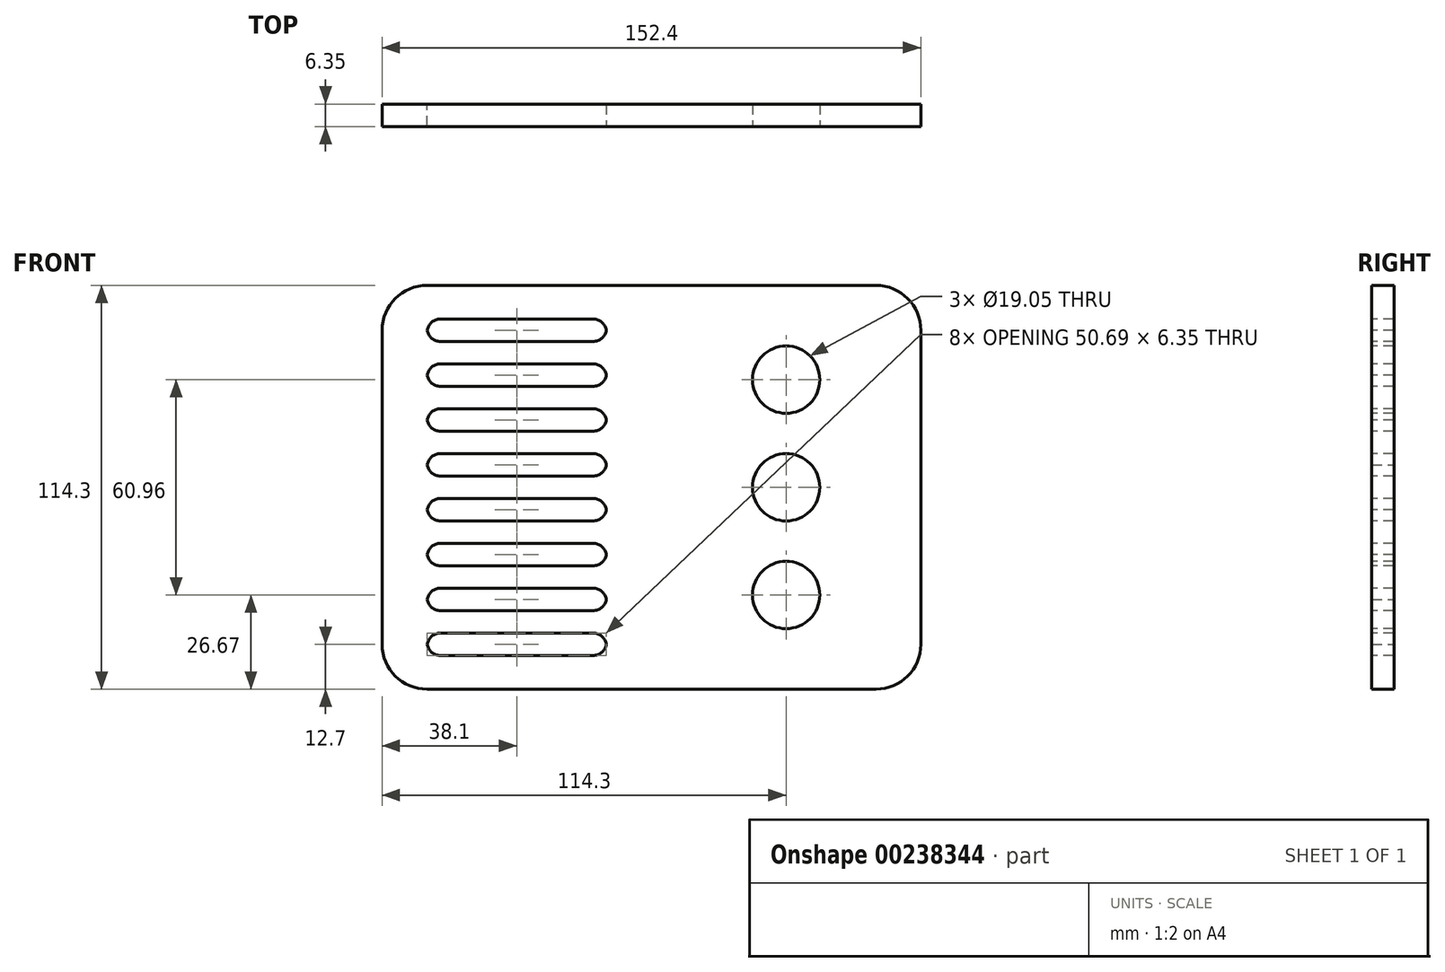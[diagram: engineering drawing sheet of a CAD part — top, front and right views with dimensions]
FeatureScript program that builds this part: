
annotation { "Feature Type Name" : "Feature", "Feature Type Description" : "" }
export const myFeature = defineFeature(function(context is Context, id is Id, definition is map)
    precondition{}
    {
        {
            var Q0;
            Q0=qCreatedBy(makeId("Front.planeOp"),FACE);
            var sketch = newSketch(context, id + "F0", { "sketchPlane" : qUnion([Q0])});
            skLineSegment(sketch, "E0.bottom", {"start": v(-76.2, 57.15) * mm, "end": v(76.2, 57.15) * mm});
            skLineSegment(sketch, "E0.top", {"start": v(-76.2, -57.15) * mm, "end": v(76.2, -57.15) * mm});
            skLineSegment(sketch, "E0.left", {"start": v(-76.2, 57.15) * mm, "end": v(-76.2, -57.15) * mm});
            skLineSegment(sketch, "E0.right", {"start": v(76.2, 57.15) * mm, "end": v(76.2, -57.15) * mm});
            skPoint(sketch, "E0.middle", {"position": v(0, 0) * mm});
            skSolve(sketch);
        }
        {
            var Q0;
            Q0=makeQuery(id+"F0.imprint","IMPRINT",FACE,{"disambiguationData":[TD([[makeQuery(id+"F0.imprint","IMPRINT",EDGE,{"derivedFrom":sQuery(id+"F0.wireOp",EDGE,"E0.bottom")}),-1.0]])]});
            extrude(context, id + "F1", {"entities" : qUnion([Q0]), "depth" : 6.35 * mm});
        }
        {
            var Q0;
            Q0=makeQuery(id+"F1.opExtrude","SWEPT_EDGE",EDGE,{"disambiguationData":[OSD([sQuery(id+"F0.wireOp",EDGE,"E0.bottom"),sQuery(id+"F0.wireOp",EDGE,"E0.left")])]});
            var Q1;
            Q1=makeQuery(id+"F1.opExtrude","SWEPT_EDGE",EDGE,{"disambiguationData":[OSD([sQuery(id+"F0.wireOp",EDGE,"E0.top"),sQuery(id+"F0.wireOp",EDGE,"E0.left")])]});
            var Q2;
            Q2=makeQuery(id+"F1.opExtrude","SWEPT_EDGE",EDGE,{"disambiguationData":[OSD([sQuery(id+"F0.wireOp",EDGE,"E0.top"),sQuery(id+"F0.wireOp",EDGE,"E0.right")])]});
            var Q3;
            Q3=makeQuery(id+"F1.opExtrude","SWEPT_EDGE",EDGE,{"disambiguationData":[OSD([sQuery(id+"F0.wireOp",EDGE,"E0.bottom"),sQuery(id+"F0.wireOp",EDGE,"E0.right")])]});
            fillet(context, id + "F2", {"entities" : qUnion([Q0, Q1, Q2, Q3]), "radius" : 12.7 * mm, "tangentPropagation" : true, "allowEdgeOverflow" : false});
        }
        {
            var Q0;
            Q0=makeQuery(id+"F1.opExtrude","CAP_FACE",FACE,{"disambiguationData":[OSD([sQuery(id+"F0.wireOp",EDGE,"E0.bottom"),sQuery(id+"F0.wireOp",EDGE,"E0.top"),sQuery(id+"F0.wireOp",EDGE,"E0.left"),sQuery(id+"F0.wireOp",EDGE,"E0.right")])],"isStart":false});
            var sketch = newSketch(context, id + "F3", { "sketchPlane" : qUnion([Q0])});
            skCircle(sketch, "E1", {"center": v(38.1, 30.48) * mm, "radius": 9.53 * mm});
            skSolve(sketch);
        }
        {
            var Q0;
            Q0=makeQuery(id+"F3.imprint","IMPRINT",FACE,{"disambiguationData":[TD([[makeQuery(id+"F3.imprint","IMPRINT",EDGE,{"derivedFrom":sQuery(id+"F3.wireOp",EDGE,"E1")}),1.0]])]});
            extrude(context, id + "F4", {"entities" : qUnion([Q0]), "operationType" : NewBodyOperationType.REMOVE, "oppositeDirection" : true, "depth" : 25.4 * mm});
        }
        {
            var Q0;
            Q0=makeQuery(id+"F1.opExtrude","CAP_FACE",FACE,{"disambiguationData":[OSD([sQuery(id+"F0.wireOp",EDGE,"E0.bottom"),sQuery(id+"F0.wireOp",EDGE,"E0.top"),sQuery(id+"F0.wireOp",EDGE,"E0.left"),sQuery(id+"F0.wireOp",EDGE,"E0.right")])],"isStart":false});
            var sketch = newSketch(context, id + "F5", { "sketchPlane" : qUnion([Q0])});
            skCircle(sketch, "E2", {"center": v(38.1, 0) * mm, "radius": 9.53 * mm});
            skSolve(sketch);
        }
        {
            var Q0;
            Q0=makeQuery(id+"F5.imprint","IMPRINT",FACE,{"disambiguationData":[TD([[makeQuery(id+"F5.imprint","IMPRINT",EDGE,{"derivedFrom":sQuery(id+"F5.wireOp",EDGE,"E2")}),1.0]])]});
            extrude(context, id + "F6", {"entities" : qUnion([Q0]), "operationType" : NewBodyOperationType.REMOVE, "oppositeDirection" : true, "depth" : 25.4 * mm});
        }
        {
            var Q0;
            Q0=makeQuery(id+"F1.opExtrude","CAP_FACE",FACE,{"disambiguationData":[OSD([sQuery(id+"F0.wireOp",EDGE,"E0.bottom"),sQuery(id+"F0.wireOp",EDGE,"E0.top"),sQuery(id+"F0.wireOp",EDGE,"E0.left"),sQuery(id+"F0.wireOp",EDGE,"E0.right")])],"isStart":false});
            var sketch = newSketch(context, id + "F7", { "sketchPlane" : qUnion([Q0])});
            skCircle(sketch, "E3", {"center": v(38.1, -30.48) * mm, "radius": 9.53 * mm});
            skSolve(sketch);
        }
        {
            var Q0;
            Q0=makeQuery(id+"F7.imprint","IMPRINT",FACE,{"disambiguationData":[TD([[makeQuery(id+"F7.imprint","IMPRINT",EDGE,{"derivedFrom":sQuery(id+"F7.wireOp",EDGE,"E3")}),1.0]])]});
            extrude(context, id + "F8", {"entities" : qUnion([Q0]), "operationType" : NewBodyOperationType.REMOVE, "oppositeDirection" : true, "depth" : 25.4 * mm});
        }
        {
            var Q0;
            Q0=makeQuery(id+"F1.opExtrude","CAP_FACE",FACE,{"disambiguationData":[OSD([sQuery(id+"F0.wireOp",EDGE,"E0.bottom"),sQuery(id+"F0.wireOp",EDGE,"E0.top"),sQuery(id+"F0.wireOp",EDGE,"E0.left"),sQuery(id+"F0.wireOp",EDGE,"E0.right")])],"isStart":false});
            var sketch = newSketch(context, id + "F9", { "sketchPlane" : qUnion([Q0])});
            skLineSegment(sketch, "E4.bottom", {"start": v(-12.7, -41.28) * mm, "end": v(-63.5, -41.28) * mm});
            skLineSegment(sketch, "E4.top", {"start": v(-12.7, -47.63) * mm, "end": v(-63.5, -47.63) * mm});
            skLineSegment(sketch, "E4.left", {"start": v(-12.7, -41.28) * mm, "end": v(-12.7, -47.63) * mm});
            skLineSegment(sketch, "E4.right", {"start": v(-63.5, -41.28) * mm, "end": v(-63.5, -47.63) * mm});
            skPoint(sketch, "E4.middle", {"position": v(-38.1, -44.45) * mm});
            skSolve(sketch);
        }
        {
            var Q0;
            Q0=makeQuery(id+"F9.imprint","IMPRINT",FACE,{"disambiguationData":[TD([[makeQuery(id+"F9.imprint","IMPRINT",EDGE,{"derivedFrom":sQuery(id+"F9.wireOp",EDGE,"E4.bottom")}),-1.0]])]});
            var sketch = newSketch(context, id + "F10", { "sketchPlane" : qUnion([Q0])});
            skLineSegment(sketch, "E5.bottom", {"start": v(-12.7, -28.58) * mm, "end": v(-63.5, -28.58) * mm});
            skLineSegment(sketch, "E5.top", {"start": v(-12.7, -34.93) * mm, "end": v(-63.5, -34.93) * mm});
            skLineSegment(sketch, "E5.left", {"start": v(-12.7, -28.58) * mm, "end": v(-12.7, -34.93) * mm});
            skLineSegment(sketch, "E5.right", {"start": v(-63.5, -28.58) * mm, "end": v(-63.5, -34.93) * mm});
            skPoint(sketch, "E5.middle", {"position": v(-38.1, -31.75) * mm});
            skSolve(sketch);
        }
        {
            var Q0;
            Q0=makeQuery(id+"F9.imprint","IMPRINT",FACE,{"disambiguationData":[TD([[makeQuery(id+"F9.imprint","IMPRINT",EDGE,{"derivedFrom":sQuery(id+"F9.wireOp",EDGE,"E4.bottom")}),-1.0]])]});
            var sketch = newSketch(context, id + "F11", { "sketchPlane" : qUnion([Q0])});
            skLineSegment(sketch, "E6.bottom", {"start": v(-12.7, -22.23) * mm, "end": v(-63.5, -22.23) * mm});
            skLineSegment(sketch, "E6.top", {"start": v(-12.7, -15.88) * mm, "end": v(-63.5, -15.88) * mm});
            skLineSegment(sketch, "E6.left", {"start": v(-12.7, -22.23) * mm, "end": v(-12.7, -15.88) * mm});
            skLineSegment(sketch, "E6.right", {"start": v(-63.5, -22.23) * mm, "end": v(-63.5, -15.88) * mm});
            skPoint(sketch, "E6.middle", {"position": v(-38.1, -19.05) * mm});
            skSolve(sketch);
        }
        {
            var Q0;
            Q0=makeQuery(id+"F9.imprint","IMPRINT",FACE,{"disambiguationData":[TD([[makeQuery(id+"F9.imprint","IMPRINT",EDGE,{"derivedFrom":sQuery(id+"F9.wireOp",EDGE,"E4.bottom")}),-1.0]])]});
            var sketch = newSketch(context, id + "F12", { "sketchPlane" : qUnion([Q0])});
            skLineSegment(sketch, "E7.bottom", {"start": v(-12.7, -9.53) * mm, "end": v(-63.5, -9.53) * mm});
            skLineSegment(sketch, "E7.top", {"start": v(-12.7, -3.18) * mm, "end": v(-63.5, -3.18) * mm});
            skLineSegment(sketch, "E7.left", {"start": v(-12.7, -9.53) * mm, "end": v(-12.7, -3.18) * mm});
            skLineSegment(sketch, "E7.right", {"start": v(-63.5, -9.53) * mm, "end": v(-63.5, -3.18) * mm});
            skPoint(sketch, "E7.middle", {"position": v(-38.1, -6.35) * mm});
            skSolve(sketch);
        }
        {
            var Q0;
            Q0=makeQuery(id+"F9.imprint","IMPRINT",FACE,{"disambiguationData":[TD([[makeQuery(id+"F9.imprint","IMPRINT",EDGE,{"derivedFrom":sQuery(id+"F9.wireOp",EDGE,"E4.bottom")}),-1.0]])]});
            var sketch = newSketch(context, id + "F13", { "sketchPlane" : qUnion([Q0])});
            skLineSegment(sketch, "E8.bottom", {"start": v(-12.7, 9.53) * mm, "end": v(-63.5, 9.52) * mm});
            skLineSegment(sketch, "E8.top", {"start": v(-12.7, 3.17) * mm, "end": v(-63.5, 3.17) * mm});
            skLineSegment(sketch, "E8.left", {"start": v(-12.7, 9.53) * mm, "end": v(-12.7, 3.17) * mm});
            skLineSegment(sketch, "E8.right", {"start": v(-63.5, 9.52) * mm, "end": v(-63.5, 3.17) * mm});
            skPoint(sketch, "E8.middle", {"position": v(-38.1, 6.35) * mm});
            skSolve(sketch);
        }
        {
            var Q0;
            Q0=makeQuery(id+"F9.imprint","IMPRINT",FACE,{"disambiguationData":[TD([[makeQuery(id+"F9.imprint","IMPRINT",EDGE,{"derivedFrom":sQuery(id+"F9.wireOp",EDGE,"E4.bottom")}),-1.0]])]});
            var sketch = newSketch(context, id + "F14", { "sketchPlane" : qUnion([Q0])});
            skLineSegment(sketch, "E9.bottom", {"start": v(-12.7, 15.88) * mm, "end": v(-63.5, 15.87) * mm});
            skLineSegment(sketch, "E9.top", {"start": v(-12.7, 22.22) * mm, "end": v(-63.5, 22.22) * mm});
            skLineSegment(sketch, "E9.left", {"start": v(-12.7, 15.88) * mm, "end": v(-12.7, 22.22) * mm});
            skLineSegment(sketch, "E9.right", {"start": v(-63.5, 15.88) * mm, "end": v(-63.5, 22.22) * mm});
            skPoint(sketch, "E9.middle", {"position": v(-38.1, 19.05) * mm});
            skSolve(sketch);
        }
        {
            var Q0;
            Q0=makeQuery(id+"F9.imprint","IMPRINT",FACE,{"disambiguationData":[TD([[makeQuery(id+"F9.imprint","IMPRINT",EDGE,{"derivedFrom":sQuery(id+"F9.wireOp",EDGE,"E4.bottom")}),-1.0]])]});
            var sketch = newSketch(context, id + "F15", { "sketchPlane" : qUnion([Q0])});
            skLineSegment(sketch, "E10.bottom", {"start": v(-12.7, 28.58) * mm, "end": v(-63.5, 28.57) * mm});
            skLineSegment(sketch, "E10.top", {"start": v(-12.7, 34.93) * mm, "end": v(-63.5, 34.92) * mm});
            skLineSegment(sketch, "E10.left", {"start": v(-12.7, 28.58) * mm, "end": v(-12.7, 34.93) * mm});
            skLineSegment(sketch, "E10.right", {"start": v(-63.5, 28.57) * mm, "end": v(-63.5, 34.92) * mm});
            skPoint(sketch, "E10.middle", {"position": v(-38.1, 31.75) * mm});
            skSolve(sketch);
        }
        {
            var Q0;
            Q0=makeQuery(id+"F9.imprint","IMPRINT",FACE,{"disambiguationData":[TD([[makeQuery(id+"F9.imprint","IMPRINT",EDGE,{"derivedFrom":sQuery(id+"F9.wireOp",EDGE,"E4.bottom")}),-1.0]])]});
            var sketch = newSketch(context, id + "F16", { "sketchPlane" : qUnion([Q0])});
            skLineSegment(sketch, "E11.bottom", {"start": v(-12.7, 41.28) * mm, "end": v(-63.5, 41.27) * mm});
            skLineSegment(sketch, "E11.top", {"start": v(-12.7, 47.63) * mm, "end": v(-63.5, 47.62) * mm});
            skLineSegment(sketch, "E11.left", {"start": v(-12.7, 41.28) * mm, "end": v(-12.7, 47.63) * mm});
            skLineSegment(sketch, "E11.right", {"start": v(-63.5, 41.27) * mm, "end": v(-63.5, 47.62) * mm});
            skPoint(sketch, "E11.middle", {"position": v(-38.1, 44.45) * mm});
            skSolve(sketch);
        }
        {
            var Q0;
            Q0=makeQuery(id+"F16.imprint","IMPRINT",FACE,{"disambiguationData":[TD([[makeQuery(id+"F16.imprint","IMPRINT",EDGE,{"derivedFrom":sQuery(id+"F16.wireOp",EDGE,"E11.bottom")}),-1.0]])]});
            var Q1;
            Q1=makeQuery(id+"F15.imprint","IMPRINT",FACE,{"disambiguationData":[TD([[makeQuery(id+"F15.imprint","IMPRINT",EDGE,{"derivedFrom":sQuery(id+"F15.wireOp",EDGE,"E10.bottom")}),-1.0]])]});
            var Q2;
            Q2=makeQuery(id+"F14.imprint","IMPRINT",FACE,{"disambiguationData":[TD([[makeQuery(id+"F14.imprint","IMPRINT",EDGE,{"derivedFrom":sQuery(id+"F14.wireOp",EDGE,"E9.bottom")}),-1.0]])]});
            var Q3;
            Q3=makeQuery(id+"F13.imprint","IMPRINT",FACE,{"disambiguationData":[TD([[makeQuery(id+"F13.imprint","IMPRINT",EDGE,{"derivedFrom":sQuery(id+"F13.wireOp",EDGE,"E8.bottom")}),1.0]])]});
            var Q4;
            Q4=makeQuery(id+"F12.imprint","IMPRINT",FACE,{"disambiguationData":[TD([[makeQuery(id+"F12.imprint","IMPRINT",EDGE,{"derivedFrom":sQuery(id+"F12.wireOp",EDGE,"E7.bottom")}),-1.0]])]});
            var Q5;
            Q5=makeQuery(id+"F11.imprint","IMPRINT",FACE,{"disambiguationData":[TD([[makeQuery(id+"F11.imprint","IMPRINT",EDGE,{"derivedFrom":sQuery(id+"F11.wireOp",EDGE,"E6.bottom")}),-1.0]])]});
            var Q6;
            Q6=makeQuery(id+"F10.imprint","IMPRINT",FACE,{"disambiguationData":[TD([[makeQuery(id+"F10.imprint","IMPRINT",EDGE,{"derivedFrom":sQuery(id+"F10.wireOp",EDGE,"E5.bottom")}),1.0]])]});
            var Q7;
            Q7=makeQuery(id+"F9.imprint","IMPRINT",FACE,{"disambiguationData":[TD([[makeQuery(id+"F9.imprint","IMPRINT",EDGE,{"derivedFrom":sQuery(id+"F9.wireOp",EDGE,"E4.bottom")}),1.0]])]});
            extrude(context, id + "F17", {"entities" : qUnion([Q0, Q1, Q2, Q3, Q4, Q5, Q6, Q7]), "operationType" : NewBodyOperationType.REMOVE, "oppositeDirection" : true, "depth" : 25.4 * mm});
        }
        {
            var Q0;
            Q0=makeQuery(id+"F17.boolean.opBoolean","COPY",EDGE,{"derivedFrom":makeQuery(id+"F17.opExtrude","SWEPT_EDGE",EDGE,{"disambiguationData":[OSD([sQuery(id+"F13.wireOp",EDGE,"E8.top"),sQuery(id+"F13.wireOp",EDGE,"E8.left")])]})});
            var Q1;
            Q1=makeQuery(id+"F17.boolean.opBoolean","COPY",EDGE,{"derivedFrom":makeQuery(id+"F17.opExtrude","SWEPT_EDGE",EDGE,{"disambiguationData":[OSD([sQuery(id+"F12.wireOp",EDGE,"E7.bottom"),sQuery(id+"F12.wireOp",EDGE,"E7.left")])]})});
            var Q2;
            Q2=makeQuery(id+"F17.boolean.opBoolean","COPY",EDGE,{"derivedFrom":makeQuery(id+"F17.opExtrude","SWEPT_EDGE",EDGE,{"disambiguationData":[OSD([sQuery(id+"F10.wireOp",EDGE,"E5.top"),sQuery(id+"F10.wireOp",EDGE,"E5.left")])]})});
            var Q3;
            Q3=makeQuery(id+"F17.boolean.opBoolean","COPY",EDGE,{"derivedFrom":makeQuery(id+"F17.opExtrude","SWEPT_EDGE",EDGE,{"disambiguationData":[OSD([sQuery(id+"F11.wireOp",EDGE,"E6.bottom"),sQuery(id+"F11.wireOp",EDGE,"E6.left")])]})});
            var Q4;
            Q4=makeQuery(id+"F17.boolean.opBoolean","COPY",EDGE,{"derivedFrom":makeQuery(id+"F17.opExtrude","SWEPT_EDGE",EDGE,{"disambiguationData":[OSD([sQuery(id+"F9.wireOp",EDGE,"E4.top"),sQuery(id+"F9.wireOp",EDGE,"E4.left")])]})});
            var Q5;
            Q5=makeQuery(id+"F17.boolean.opBoolean","COPY",EDGE,{"derivedFrom":makeQuery(id+"F17.opExtrude","SWEPT_EDGE",EDGE,{"disambiguationData":[OSD([sQuery(id+"F14.wireOp",EDGE,"E9.bottom"),sQuery(id+"F14.wireOp",EDGE,"E9.left")])]})});
            var Q6;
            Q6=makeQuery(id+"F17.boolean.opBoolean","COPY",EDGE,{"derivedFrom":makeQuery(id+"F17.opExtrude","SWEPT_EDGE",EDGE,{"disambiguationData":[OSD([sQuery(id+"F15.wireOp",EDGE,"E10.bottom"),sQuery(id+"F15.wireOp",EDGE,"E10.left")])]})});
            var Q7;
            Q7=makeQuery(id+"F17.boolean.opBoolean","COPY",EDGE,{"derivedFrom":makeQuery(id+"F17.opExtrude","SWEPT_EDGE",EDGE,{"disambiguationData":[OSD([sQuery(id+"F16.wireOp",EDGE,"E11.bottom"),sQuery(id+"F16.wireOp",EDGE,"E11.left")])]})});
            var Q8;
            Q8=makeQuery(id+"F17.boolean.opBoolean","COPY",EDGE,{"derivedFrom":makeQuery(id+"F17.opExtrude","SWEPT_EDGE",EDGE,{"disambiguationData":[OSD([sQuery(id+"F9.wireOp",EDGE,"E4.bottom"),sQuery(id+"F9.wireOp",EDGE,"E4.left")])]})});
            var Q9;
            Q9=makeQuery(id+"F17.boolean.opBoolean","COPY",EDGE,{"derivedFrom":makeQuery(id+"F17.opExtrude","SWEPT_EDGE",EDGE,{"disambiguationData":[OSD([sQuery(id+"F10.wireOp",EDGE,"E5.bottom"),sQuery(id+"F10.wireOp",EDGE,"E5.left")])]})});
            var Q10;
            Q10=makeQuery(id+"F17.boolean.opBoolean","COPY",EDGE,{"derivedFrom":makeQuery(id+"F17.opExtrude","SWEPT_EDGE",EDGE,{"disambiguationData":[OSD([sQuery(id+"F11.wireOp",EDGE,"E6.top"),sQuery(id+"F11.wireOp",EDGE,"E6.left")])]})});
            var Q11;
            Q11=makeQuery(id+"F17.boolean.opBoolean","COPY",EDGE,{"derivedFrom":makeQuery(id+"F17.opExtrude","SWEPT_EDGE",EDGE,{"disambiguationData":[OSD([sQuery(id+"F12.wireOp",EDGE,"E7.top"),sQuery(id+"F12.wireOp",EDGE,"E7.left")])]})});
            var Q12;
            Q12=makeQuery(id+"F17.boolean.opBoolean","COPY",EDGE,{"derivedFrom":makeQuery(id+"F17.opExtrude","SWEPT_EDGE",EDGE,{"disambiguationData":[OSD([sQuery(id+"F13.wireOp",EDGE,"E8.bottom"),sQuery(id+"F13.wireOp",EDGE,"E8.left")])]})});
            var Q13;
            Q13=makeQuery(id+"F17.boolean.opBoolean","COPY",EDGE,{"derivedFrom":makeQuery(id+"F17.opExtrude","SWEPT_EDGE",EDGE,{"disambiguationData":[OSD([sQuery(id+"F14.wireOp",EDGE,"E9.top"),sQuery(id+"F14.wireOp",EDGE,"E9.left")])]})});
            var Q14;
            Q14=makeQuery(id+"F17.boolean.opBoolean","COPY",EDGE,{"derivedFrom":makeQuery(id+"F17.opExtrude","SWEPT_EDGE",EDGE,{"disambiguationData":[OSD([sQuery(id+"F15.wireOp",EDGE,"E10.top"),sQuery(id+"F15.wireOp",EDGE,"E10.left")])]})});
            var Q15;
            Q15=makeQuery(id+"F17.boolean.opBoolean","COPY",EDGE,{"derivedFrom":makeQuery(id+"F17.opExtrude","SWEPT_EDGE",EDGE,{"disambiguationData":[OSD([sQuery(id+"F16.wireOp",EDGE,"E11.top"),sQuery(id+"F16.wireOp",EDGE,"E11.left")])]})});
            fillet(context, id + "F18", {"entities" : qUnion([Q0, Q1, Q2, Q3, Q4, Q5, Q6, Q7, Q8, Q9, Q10, Q11, Q12, Q13, Q14, Q15]), "radius" : 3.8 * mm, "tangentPropagation" : true, "allowEdgeOverflow" : false});
        }
        {
            var Q0;
            Q0=makeQuery(id+"F17.boolean.opBoolean","COPY",EDGE,{"derivedFrom":makeQuery(id+"F17.opExtrude","SWEPT_EDGE",EDGE,{"disambiguationData":[OSD([sQuery(id+"F16.wireOp",EDGE,"E11.top"),sQuery(id+"F16.wireOp",EDGE,"E11.right")])]})});
            var Q1;
            Q1=makeQuery(id+"F17.boolean.opBoolean","COPY",EDGE,{"derivedFrom":makeQuery(id+"F17.opExtrude","SWEPT_EDGE",EDGE,{"disambiguationData":[OSD([sQuery(id+"F15.wireOp",EDGE,"E10.top"),sQuery(id+"F15.wireOp",EDGE,"E10.right")])]})});
            var Q2;
            Q2=makeQuery(id+"F17.boolean.opBoolean","COPY",EDGE,{"derivedFrom":makeQuery(id+"F17.opExtrude","SWEPT_EDGE",EDGE,{"disambiguationData":[OSD([sQuery(id+"F14.wireOp",EDGE,"E9.top"),sQuery(id+"F14.wireOp",EDGE,"E9.right")])]})});
            var Q3;
            Q3=makeQuery(id+"F17.boolean.opBoolean","COPY",EDGE,{"derivedFrom":makeQuery(id+"F17.opExtrude","SWEPT_EDGE",EDGE,{"disambiguationData":[OSD([sQuery(id+"F13.wireOp",EDGE,"E8.bottom"),sQuery(id+"F13.wireOp",EDGE,"E8.right")])]})});
            var Q4;
            Q4=makeQuery(id+"F17.boolean.opBoolean","COPY",EDGE,{"derivedFrom":makeQuery(id+"F17.opExtrude","SWEPT_EDGE",EDGE,{"disambiguationData":[OSD([sQuery(id+"F12.wireOp",EDGE,"E7.top"),sQuery(id+"F12.wireOp",EDGE,"E7.right")])]})});
            var Q5;
            Q5=makeQuery(id+"F17.boolean.opBoolean","COPY",EDGE,{"derivedFrom":makeQuery(id+"F17.opExtrude","SWEPT_EDGE",EDGE,{"disambiguationData":[OSD([sQuery(id+"F11.wireOp",EDGE,"E6.top"),sQuery(id+"F11.wireOp",EDGE,"E6.right")])]})});
            var Q6;
            Q6=makeQuery(id+"F17.boolean.opBoolean","COPY",EDGE,{"derivedFrom":makeQuery(id+"F17.opExtrude","SWEPT_EDGE",EDGE,{"disambiguationData":[OSD([sQuery(id+"F10.wireOp",EDGE,"E5.bottom"),sQuery(id+"F10.wireOp",EDGE,"E5.right")])]})});
            var Q7;
            Q7=makeQuery(id+"F17.boolean.opBoolean","COPY",EDGE,{"derivedFrom":makeQuery(id+"F17.opExtrude","SWEPT_EDGE",EDGE,{"disambiguationData":[OSD([sQuery(id+"F9.wireOp",EDGE,"E4.bottom"),sQuery(id+"F9.wireOp",EDGE,"E4.right")])]})});
            var Q8;
            Q8=makeQuery(id+"F17.boolean.opBoolean","COPY",EDGE,{"derivedFrom":makeQuery(id+"F17.opExtrude","SWEPT_EDGE",EDGE,{"disambiguationData":[OSD([sQuery(id+"F16.wireOp",EDGE,"E11.bottom"),sQuery(id+"F16.wireOp",EDGE,"E11.right")])]})});
            var Q9;
            Q9=makeQuery(id+"F17.boolean.opBoolean","COPY",EDGE,{"derivedFrom":makeQuery(id+"F17.opExtrude","SWEPT_EDGE",EDGE,{"disambiguationData":[OSD([sQuery(id+"F15.wireOp",EDGE,"E10.bottom"),sQuery(id+"F15.wireOp",EDGE,"E10.right")])]})});
            var Q10;
            Q10=makeQuery(id+"F17.boolean.opBoolean","COPY",EDGE,{"derivedFrom":makeQuery(id+"F17.opExtrude","SWEPT_EDGE",EDGE,{"disambiguationData":[OSD([sQuery(id+"F14.wireOp",EDGE,"E9.bottom"),sQuery(id+"F14.wireOp",EDGE,"E9.right")])]})});
            var Q11;
            Q11=makeQuery(id+"F17.boolean.opBoolean","COPY",EDGE,{"derivedFrom":makeQuery(id+"F17.opExtrude","SWEPT_EDGE",EDGE,{"disambiguationData":[OSD([sQuery(id+"F13.wireOp",EDGE,"E8.top"),sQuery(id+"F13.wireOp",EDGE,"E8.right")])]})});
            var Q12;
            Q12=makeQuery(id+"F17.boolean.opBoolean","COPY",EDGE,{"derivedFrom":makeQuery(id+"F17.opExtrude","SWEPT_EDGE",EDGE,{"disambiguationData":[OSD([sQuery(id+"F12.wireOp",EDGE,"E7.bottom"),sQuery(id+"F12.wireOp",EDGE,"E7.right")])]})});
            var Q13;
            Q13=makeQuery(id+"F17.boolean.opBoolean","COPY",EDGE,{"derivedFrom":makeQuery(id+"F17.opExtrude","SWEPT_EDGE",EDGE,{"disambiguationData":[OSD([sQuery(id+"F11.wireOp",EDGE,"E6.bottom"),sQuery(id+"F11.wireOp",EDGE,"E6.right")])]})});
            var Q14;
            Q14=makeQuery(id+"F17.boolean.opBoolean","COPY",EDGE,{"derivedFrom":makeQuery(id+"F17.opExtrude","SWEPT_EDGE",EDGE,{"disambiguationData":[OSD([sQuery(id+"F10.wireOp",EDGE,"E5.top"),sQuery(id+"F10.wireOp",EDGE,"E5.right")])]})});
            var Q15;
            Q15=makeQuery(id+"F17.boolean.opBoolean","COPY",EDGE,{"derivedFrom":makeQuery(id+"F17.opExtrude","SWEPT_EDGE",EDGE,{"disambiguationData":[OSD([sQuery(id+"F9.wireOp",EDGE,"E4.top"),sQuery(id+"F9.wireOp",EDGE,"E4.right")])]})});
            fillet(context, id + "F19", {"entities" : qUnion([Q0, Q1, Q2, Q3, Q4, Q5, Q6, Q7, Q8, Q9, Q10, Q11, Q12, Q13, Q14, Q15]), "radius" : 3.8 * mm, "tangentPropagation" : true, "allowEdgeOverflow" : false});
        }
    });
